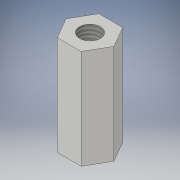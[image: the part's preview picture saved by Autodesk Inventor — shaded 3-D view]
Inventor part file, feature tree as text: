
AUTODESK INVENTOR PART (.ipt)
format: ipt  version: 2017.3 (Build 213257000, 257)  size: 102,912 bytes
history: native  units: mm
features: sketch x2, extrude x1, hole x1, thread x1
ambient origin geometry x8: Origin, YZ Plane, XZ Plane, XY Plane, X Axis, Y Axis, Z Axis, Center Point
bodies: Volumenkörper1 (feature_tree)
feature tree (5):
  extrude  "Extrusion1"  TaperAngle=120.0deg  [1 undecoded]
  hole  "Bohrung1"  [1 undecoded]
  thread  "Gewinde1"  [1 undecoded]
  sketch  "Skizze1"  dims[d3=120.0deg d4=120.0deg]
  sketch  "Skizze2"  dims[d5=120.0deg d6=5.0mm d7=12.0mm d8=0.0mm d9=2.5mm d10=5.0mm d11=4.0mm d12=2.0mm d13=90.0deg d14=7.6mm d15=20.594885mm d16=10.0mm d17=0.0mm]
note: 3 required parameter values undecoded (feature->parameter linkage not recoverable at this tier; creation-order binding heuristic only, values carry confidence <= 0.55)
